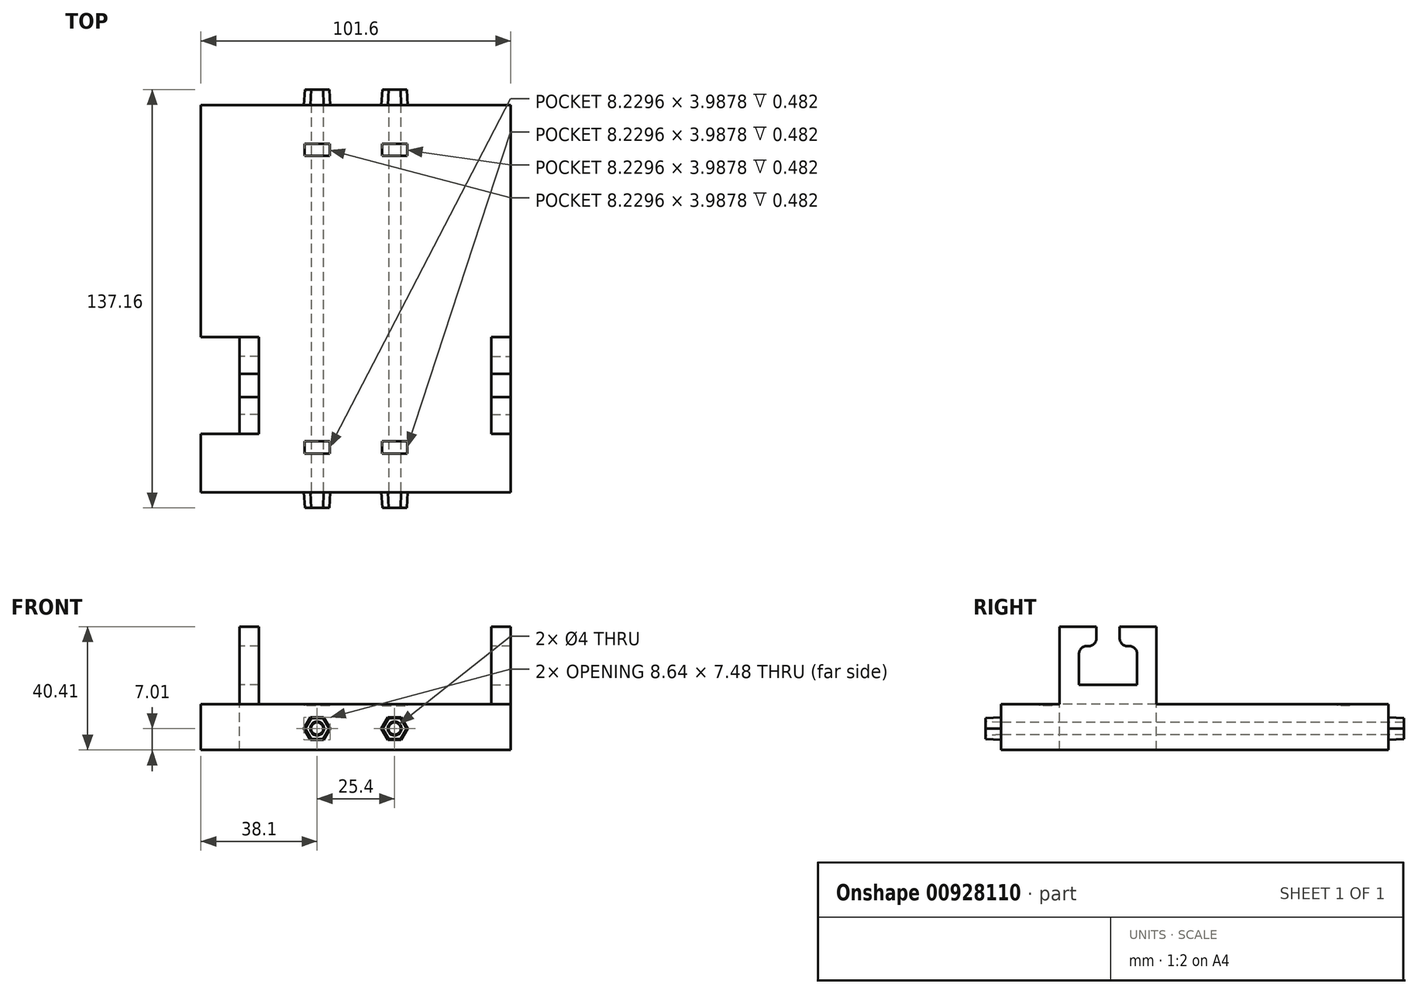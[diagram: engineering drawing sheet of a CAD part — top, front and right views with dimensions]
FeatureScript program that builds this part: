
annotation { "Feature Type Name" : "Feature", "Feature Type Description" : "" }
export const myFeature = defineFeature(function(context is Context, id is Id, definition is map)
    precondition{}
    {
        {
            var Q0;
            Q0=qCreatedBy(makeId("Top.planeOp"),FACE);
            var sketch = newSketch(context, id + "F0", { "sketchPlane" : qUnion([Q0])});
            skLineSegment(sketch, "E0.bottom", {"start": v(-50.8, 0) * mm, "end": v(50.8, 0) * mm});
            skLineSegment(sketch, "E0.top", {"start": v(-50.8, -127) * mm, "end": v(50.8, -127) * mm});
            skLineSegment(sketch, "E0.left", {"start": v(-50.8, 0) * mm, "end": v(-50.8, -127) * mm});
            skLineSegment(sketch, "E0.right", {"start": v(50.8, 0) * mm, "end": v(50.8, -127) * mm});
            skSolve(sketch);
        }
        {
            var Q0;
            Q0 = qSketchRegion(id + "F0", true);
            extrude(context, id + "F1", {"entities" : qUnion([Q0]), "depth" : 15 * mm, "offsetDistance" : 25.4 * mm});
        }
        {
            var Q0;
            Q0=makeQuery(id+"F1.opExtrude","SWEPT_FACE",FACE,{"disambiguationData":[OSD([sQuery(id+"F0.wireOp",EDGE,"E0.bottom")])]});
            var sketch = newSketch(context, id + "F2", { "sketchPlane" : qUnion([Q0])});
            skCircle(sketch, "E1", {"center": v(12.7, 7.01) * mm, "radius": 2 * mm});
            skCircle(sketch, "E2", {"center": v(-12.7, 7.01) * mm, "radius": 2 * mm});
            skPoint(sketch, "E3", {"position": v(-50.8, 7.5) * mm});
            skLineSegment(sketch, "E4", {"start": v(-12.7, 7.01) * mm, "end": v(12.7, 7.01) * mm, "construction": true});
            skLineSegment(sketch, "E5", {"start": v(0, 7.01) * mm, "end": v(0, 15.01) * mm, "construction": true});
            skSolve(sketch);
        }
        {
            var Q0;
            Q0=makeQuery(id+"F1.opExtrude","SWEPT_FACE",FACE,{"disambiguationData":[OSD([sQuery(id+"F0.wireOp",EDGE,"E0.bottom")])]});
            var sketch = newSketch(context, id + "F3", { "sketchPlane" : qUnion([Q0])});
            skCircle(sketch, "E6.cCircle", {"center": v(-12.7, 7.01) * mm, "radius": 3.74 * mm, "construction": true});
            skLineSegment(sketch, "E6.0", {"start": v(-8.38, 7.01) * mm, "end": v(-10.54, 3.27) * mm});
            skLineSegment(sketch, "E6.1", {"start": v(-10.54, 3.27) * mm, "end": v(-14.86, 3.27) * mm});
            skLineSegment(sketch, "E6.2", {"start": v(-14.86, 3.27) * mm, "end": v(-17.02, 7.01) * mm});
            skLineSegment(sketch, "E6.3", {"start": v(-17.02, 7.01) * mm, "end": v(-14.86, 10.75) * mm});
            skLineSegment(sketch, "E6.4", {"start": v(-14.86, 10.75) * mm, "end": v(-10.54, 10.75) * mm});
            skLineSegment(sketch, "E6.5", {"start": v(-10.54, 10.75) * mm, "end": v(-8.38, 7.01) * mm});
            skPoint(sketch, "E6.0.midPoint", {"position": v(-9.46, 5.14) * mm});
            skCircle(sketch, "E7.cCircle", {"center": v(12.7, 7.01) * mm, "radius": 3.74 * mm, "construction": true});
            skLineSegment(sketch, "E7.0", {"start": v(17.02, 7.01) * mm, "end": v(14.86, 3.27) * mm});
            skLineSegment(sketch, "E7.1", {"start": v(14.86, 3.27) * mm, "end": v(10.54, 3.27) * mm});
            skLineSegment(sketch, "E7.2", {"start": v(10.54, 3.27) * mm, "end": v(8.38, 7.01) * mm});
            skLineSegment(sketch, "E7.3", {"start": v(8.38, 7.01) * mm, "end": v(10.54, 10.75) * mm});
            skLineSegment(sketch, "E7.4", {"start": v(10.54, 10.75) * mm, "end": v(14.86, 10.75) * mm});
            skLineSegment(sketch, "E7.5", {"start": v(14.86, 10.75) * mm, "end": v(17.02, 7.01) * mm});
            skPoint(sketch, "E7.0.midPoint", {"position": v(15.94, 5.14) * mm});
            skSolve(sketch);
        }
        {
            var Q0;
            Q0=makeQuery(id+"F1.opExtrude","SWEPT_FACE",FACE,{"disambiguationData":[OSD([sQuery(id+"F0.wireOp",EDGE,"E0.top")])]});
            var sketch = newSketch(context, id + "F4", { "sketchPlane" : qUnion([Q0])});
            skCircle(sketch, "E8.cCircle", {"center": v(-12.7, 7.01) * mm, "radius": 3.74 * mm, "construction": true});
            skLineSegment(sketch, "E8.0", {"start": v(-10.54, 3.27) * mm, "end": v(-14.86, 3.27) * mm});
            skLineSegment(sketch, "E8.1", {"start": v(-14.86, 3.27) * mm, "end": v(-17.02, 7.01) * mm});
            skLineSegment(sketch, "E8.2", {"start": v(-17.02, 7.01) * mm, "end": v(-14.86, 10.75) * mm});
            skLineSegment(sketch, "E8.3", {"start": v(-14.86, 10.75) * mm, "end": v(-10.54, 10.75) * mm});
            skLineSegment(sketch, "E8.4", {"start": v(-10.54, 10.75) * mm, "end": v(-8.38, 7.01) * mm});
            skLineSegment(sketch, "E8.5", {"start": v(-8.38, 7.01) * mm, "end": v(-10.54, 3.27) * mm});
            skPoint(sketch, "E8.0.midPoint", {"position": v(-12.7, 3.27) * mm});
            skCircle(sketch, "E9.cCircle", {"center": v(12.7, 7.01) * mm, "radius": 3.74 * mm, "construction": true});
            skLineSegment(sketch, "E9.0", {"start": v(17.02, 7.01) * mm, "end": v(14.86, 3.27) * mm});
            skLineSegment(sketch, "E9.1", {"start": v(14.86, 3.27) * mm, "end": v(10.54, 3.27) * mm});
            skLineSegment(sketch, "E9.2", {"start": v(10.54, 3.27) * mm, "end": v(8.38, 7.01) * mm});
            skLineSegment(sketch, "E9.3", {"start": v(8.38, 7.01) * mm, "end": v(10.54, 10.75) * mm});
            skLineSegment(sketch, "E9.4", {"start": v(10.54, 10.75) * mm, "end": v(14.86, 10.75) * mm});
            skLineSegment(sketch, "E9.5", {"start": v(14.86, 10.75) * mm, "end": v(17.02, 7.01) * mm});
            skPoint(sketch, "E9.0.midPoint", {"position": v(15.94, 5.14) * mm});
            skCircle(sketch, "E10", {"center": v(12.7, 7.01) * mm, "radius": 2 * mm});
            skCircle(sketch, "E11", {"center": v(-12.7, 7.01) * mm, "radius": 2 * mm});
            skPoint(sketch, "E12", {"position": v(-6.45, -15) * mm});
            skLineSegment(sketch, "E13", {"start": v(-12.7, 7.01) * mm, "end": v(12.7, 7.01) * mm, "construction": true});
            skLineSegment(sketch, "E14", {"start": v(0, 7.01) * mm, "end": v(0, 15.01) * mm, "construction": true});
            skSolve(sketch);
        }
        {
            var Q0;
            Q0 = qSketchRegion(id + "F3", true);
            extrude(context, id + "F5", {"entities" : qUnion([Q0]), "operationType" : NewBodyOperationType.ADD, "depth" : 5.08 * mm, "offsetDistance" : 25.4 * mm, "hasDraft" : true, "draftAngle" : 3 * degree, "draftPullDirection" : true});
        }
        {
            var Q0;
            Q0 = qSketchRegion(id + "F4", true);
            extrude(context, id + "F6", {"entities" : qUnion([Q0]), "operationType" : NewBodyOperationType.ADD, "depth" : 5.08 * mm, "offsetDistance" : 25.4 * mm, "hasDraft" : true, "draftAngle" : 3 * degree, "draftPullDirection" : true});
        }
        {
            var Q0;
            Q0 = qSketchRegion(id + "F2", true);
            extrude(context, id + "F7", {"entities" : qUnion([Q0]), "operationType" : NewBodyOperationType.REMOVE, "endBound" : BoundingType.SYMMETRIC, "depth" : 304.8 * mm, "offsetDistance" : 25.4 * mm});
        }
        {
            var Q0;
            Q0=makeQuery(id+"F1.opExtrude","CAP_FACE",FACE,{"disambiguationData":[OSD([sQuery(id+"F0.wireOp",EDGE,"E0.bottom"),sQuery(id+"F0.wireOp",EDGE,"E0.top"),sQuery(id+"F0.wireOp",EDGE,"E0.left"),sQuery(id+"F0.wireOp",EDGE,"E0.right")])],"isStart":false});
            var sketch = newSketch(context, id + "F8", { "sketchPlane" : qUnion([Q0])});
            skLineSegment(sketch, "E15.bottom", {"start": v(-8.59, -110.31) * mm, "end": v(-16.81, -110.31) * mm});
            skLineSegment(sketch, "E15.top", {"start": v(-8.59, -114.3) * mm, "end": v(-16.81, -114.3) * mm});
            skLineSegment(sketch, "E15.left", {"start": v(-8.59, -110.31) * mm, "end": v(-8.59, -114.3) * mm});
            skLineSegment(sketch, "E15.right", {"start": v(-16.81, -110.31) * mm, "end": v(-16.81, -114.3) * mm});
            skPoint(sketch, "E15.middle", {"position": v(-12.7, -112.3) * mm});
            skLineSegment(sketch, "E16.bottom", {"start": v(8.59, -110.31) * mm, "end": v(16.81, -110.31) * mm});
            skLineSegment(sketch, "E16.top", {"start": v(8.59, -114.3) * mm, "end": v(16.81, -114.3) * mm});
            skLineSegment(sketch, "E16.left", {"start": v(8.59, -110.31) * mm, "end": v(8.59, -114.3) * mm});
            skLineSegment(sketch, "E16.right", {"start": v(16.81, -110.31) * mm, "end": v(16.81, -114.3) * mm});
            skPoint(sketch, "E16.middle", {"position": v(12.7, -112.3) * mm});
            skLineSegment(sketch, "E17.bottom", {"start": v(8.59, -12.7) * mm, "end": v(16.81, -12.7) * mm});
            skLineSegment(sketch, "E17.top", {"start": v(8.59, -16.69) * mm, "end": v(16.81, -16.69) * mm});
            skLineSegment(sketch, "E17.left", {"start": v(8.59, -12.7) * mm, "end": v(8.59, -16.69) * mm});
            skLineSegment(sketch, "E17.right", {"start": v(16.81, -12.7) * mm, "end": v(16.81, -16.69) * mm});
            skPoint(sketch, "E17.middle", {"position": v(12.7, -14.7) * mm});
            skLineSegment(sketch, "E18.bottom", {"start": v(-8.59, -12.7) * mm, "end": v(-16.81, -12.7) * mm});
            skLineSegment(sketch, "E18.top", {"start": v(-8.59, -16.69) * mm, "end": v(-16.81, -16.69) * mm});
            skLineSegment(sketch, "E18.left", {"start": v(-8.59, -12.7) * mm, "end": v(-8.59, -16.69) * mm});
            skLineSegment(sketch, "E18.right", {"start": v(-16.81, -12.7) * mm, "end": v(-16.81, -16.69) * mm});
            skPoint(sketch, "E18.middle", {"position": v(-12.7, -14.7) * mm});
            skLineSegment(sketch, "E19", {"start": v(0, -127) * mm, "end": v(0, 0) * mm});
            skSolve(sketch);
        }
        {
            var Q0;
            Q0 = qSketchRegion(id + "F8", true);
            extrude(context, id + "F9", {"entities" : qUnion([Q0]), "operationType" : NewBodyOperationType.REMOVE, "oppositeDirection" : true, "depth" : ((.374 / 2) + (.591 / 2)) * mm, "offsetDistance" : 25.4 * mm});
        }
        {
            var Q0;
            Q0=makeQuery(id+"F1.opExtrude","SWEPT_FACE",FACE,{"disambiguationData":[OSD([sQuery(id+"F0.wireOp",EDGE,"E0.right")])]});
            var sketch = newSketch(context, id + "F10", { "sketchPlane" : qUnion([Q0])});
            skLineSegment(sketch, "E20.bottom", {"start": v(-76.1, 0) * mm, "end": v(-107.85, 0) * mm});
            skLineSegment(sketch, "E20.top", {"start": v(-76.1, 40.41) * mm, "end": v(-107.85, 40.41) * mm});
            skLineSegment(sketch, "E20.left", {"start": v(-76.1, 0) * mm, "end": v(-76.1, 40.41) * mm});
            skLineSegment(sketch, "E20.right", {"start": v(-107.85, 0) * mm, "end": v(-107.85, 40.41) * mm});
            skSolve(sketch);
        }
        {
            var Q0;
            Q0 = qSketchRegion(id + "F10", true);
            extrude(context, id + "F11", {"entities" : qUnion([Q0]), "operationType" : NewBodyOperationType.ADD, "oppositeDirection" : true, "depth" : 6.35 * mm, "offsetDistance" : 25.4 * mm});
        }
        {
            var Q0;
            Q0=makeQuery(id+"F11.boolean.opBoolean","MERGE",FACE,{"derivedFrom":[makeQuery(id+"F1.opExtrude","SWEPT_FACE",FACE,{"disambiguationData":[OSD([sQuery(id+"F0.wireOp",EDGE,"E0.right")])]}),makeQuery(id+"F11.opExtrude","CAP_FACE",FACE,{"disambiguationData":[OSD([sQuery(id+"F10.wireOp",EDGE,"E20.bottom"),sQuery(id+"F10.wireOp",EDGE,"E20.top"),sQuery(id+"F10.wireOp",EDGE,"E20.left"),sQuery(id+"F10.wireOp",EDGE,"E20.right")])],"isStart":true})]});
            var sketch = newSketch(context, id + "F12", { "sketchPlane" : qUnion([Q0])});
            skLineSegment(sketch, "E21.bottom", {"start": v(-101.5, 34.06) * mm, "end": v(-82.45, 34.06) * mm});
            skLineSegment(sketch, "E21.top", {"start": v(-101.5, 21.36) * mm, "end": v(-82.45, 21.36) * mm});
            skLineSegment(sketch, "E21.left", {"start": v(-101.5, 34.06) * mm, "end": v(-101.5, 21.36) * mm});
            skLineSegment(sketch, "E21.right", {"start": v(-82.45, 34.06) * mm, "end": v(-82.45, 21.36) * mm});
            skLineSegment(sketch, "E22", {"start": v(-101.5, 27.71) * mm, "end": v(-107.85, 27.71) * mm});
            skLineSegment(sketch, "E23", {"start": v(-82.45, 27.71) * mm, "end": v(-76.1, 27.71) * mm});
            skSolve(sketch);
        }
        {
            var Q0;
            Q0 = qSketchRegion(id + "F12", true);
            extrude(context, id + "F13", {"entities" : qUnion([Q0]), "operationType" : NewBodyOperationType.REMOVE, "oppositeDirection" : true, "depth" : 25.4 * mm, "offsetDistance" : 25.4 * mm});
        }
        {
            var Q0;
            Q0=makeQuery(id+"F11.boolean.opBoolean","MERGE",FACE,{"derivedFrom":[makeQuery(id+"F1.opExtrude","SWEPT_FACE",FACE,{"disambiguationData":[OSD([sQuery(id+"F0.wireOp",EDGE,"E0.right")])]}),makeQuery(id+"F11.opExtrude","CAP_FACE",FACE,{"disambiguationData":[OSD([sQuery(id+"F10.wireOp",EDGE,"E20.bottom"),sQuery(id+"F10.wireOp",EDGE,"E20.top"),sQuery(id+"F10.wireOp",EDGE,"E20.left"),sQuery(id+"F10.wireOp",EDGE,"E20.right")])],"isStart":true})]});
            var sketch = newSketch(context, id + "F14", { "sketchPlane" : qUnion([Q0])});
            skLineSegment(sketch, "E24", {"start": v(-82.45, 34.06) * mm, "end": v(-101.5, 21.36) * mm});
            skLineSegment(sketch, "E25", {"start": v(-101.5, 34.06) * mm, "end": v(-91.97, 27.71) * mm});
            skLineSegment(sketch, "E26", {"start": v(-91.97, 27.71) * mm, "end": v(-82.45, 21.36) * mm});
            skSolve(sketch);
        }
        {
            var Q0;
            Q0=makeQuery(id+"F1.opExtrude","CAP_FACE",FACE,{"disambiguationData":[OSD([sQuery(id+"F0.wireOp",EDGE,"E0.bottom"),sQuery(id+"F0.wireOp",EDGE,"E0.top"),sQuery(id+"F0.wireOp",EDGE,"E0.left"),sQuery(id+"F0.wireOp",EDGE,"E0.right")])],"isStart":false});
            var sketch = newSketch(context, id + "F15", { "sketchPlane" : qUnion([Q0])});
            skLineSegment(sketch, "E27.bottom", {"start": v(-50.8, -107.85) * mm, "end": v(-38.1, -107.85) * mm});
            skLineSegment(sketch, "E27.top", {"start": v(-50.8, -76.1) * mm, "end": v(-38.1, -76.1) * mm});
            skLineSegment(sketch, "E27.left", {"start": v(-50.8, -107.85) * mm, "end": v(-50.8, -76.1) * mm});
            skLineSegment(sketch, "E27.right", {"start": v(-38.1, -107.85) * mm, "end": v(-38.1, -76.1) * mm});
            skSolve(sketch);
        }
        {
            var Q0;
            Q0 = qSketchRegion(id + "F15", true);
            extrude(context, id + "F16", {"entities" : qUnion([Q0]), "operationType" : NewBodyOperationType.REMOVE, "endBound" : BoundingType.SYMMETRIC, "oppositeDirection" : true, "depth" : 50.8 * mm, "offsetDistance" : 25.4 * mm});
        }
        {
            var Q0;
            Q0=makeQuery(id+"F1.opExtrude","CAP_FACE",FACE,{"disambiguationData":[OSD([sQuery(id+"F0.wireOp",EDGE,"E0.bottom"),sQuery(id+"F0.wireOp",EDGE,"E0.top"),sQuery(id+"F0.wireOp",EDGE,"E0.left"),sQuery(id+"F0.wireOp",EDGE,"E0.right")])],"isStart":false});
            var sketch = newSketch(context, id + "F17", { "sketchPlane" : qUnion([Q0])});
            skLineSegment(sketch, "E28.bottom", {"start": v(-38.1, -76.1) * mm, "end": v(-31.75, -76.1) * mm});
            skLineSegment(sketch, "E28.top", {"start": v(-38.1, -107.85) * mm, "end": v(-31.75, -107.85) * mm});
            skLineSegment(sketch, "E28.left", {"start": v(-38.1, -76.1) * mm, "end": v(-38.1, -107.85) * mm});
            skLineSegment(sketch, "E28.right", {"start": v(-31.75, -76.1) * mm, "end": v(-31.75, -107.85) * mm});
            skSolve(sketch);
        }
        {
            var Q0;
            Q0 = qSketchRegion(id + "F17", true);
            var Q1;
            Q1=makeQuery(id+"F11.opExtrude","SWEPT_FACE",FACE,{"disambiguationData":[OSD([sQuery(id+"F10.wireOp",EDGE,"E20.top")])]});
            extrude(context, id + "F18", {"entities" : qUnion([Q0]), "operationType" : NewBodyOperationType.ADD, "endBound" : BoundingType.UP_TO_SURFACE, "depth" : 25.4 * mm, "endBoundEntityFace" : qUnion([Q1]), "offsetDistance" : 25.4 * mm});
        }
        {
            var Q0;
            Q0=makeQuery(id+"F18.boolean.opBoolean","MERGE",FACE,{"derivedFrom":[makeQuery(id+"F16.boolean.opBoolean","COPY",FACE,{"derivedFrom":makeQuery(id+"F16.opExtrude","SWEPT_FACE",FACE,{"disambiguationData":[OSD([sQuery(id+"F15.wireOp",EDGE,"E27.right")])]})}),makeQuery(id+"F18.opExtrude","SWEPT_FACE",FACE,{"disambiguationData":[OSD([sQuery(id+"F17.wireOp",EDGE,"E28.left")])]})]});
            var sketch = newSketch(context, id + "F19", { "sketchPlane" : qUnion([Q0])});
            skLineSegment(sketch, "E29.bottom", {"start": v(82.45, 34.06) * mm, "end": v(101.5, 34.06) * mm});
            skLineSegment(sketch, "E29.top", {"start": v(82.45, 21.36) * mm, "end": v(101.5, 21.36) * mm});
            skLineSegment(sketch, "E29.left", {"start": v(82.45, 34.06) * mm, "end": v(82.45, 21.36) * mm});
            skLineSegment(sketch, "E29.right", {"start": v(101.5, 34.06) * mm, "end": v(101.5, 21.36) * mm});
            skSolve(sketch);
        }
        {
            var Q0;
            Q0 = qSketchRegion(id + "F19", true);
            extrude(context, id + "F20", {"entities" : qUnion([Q0]), "operationType" : NewBodyOperationType.REMOVE, "oppositeDirection" : true, "depth" : 25.4 * mm, "offsetDistance" : 25.4 * mm});
        }
        {
            var Q0;
            Q0=makeQuery(id+"F18.opExtrude","CAP_FACE",FACE,{"disambiguationData":[OSD([sQuery(id+"F17.wireOp",EDGE,"E28.bottom"),sQuery(id+"F17.wireOp",EDGE,"E28.top"),sQuery(id+"F17.wireOp",EDGE,"E28.left"),sQuery(id+"F17.wireOp",EDGE,"E28.right")])],"isStart":false});
            var sketch = newSketch(context, id + "F21", { "sketchPlane" : qUnion([Q0])});
            skLineSegment(sketch, "E30.bottom", {"start": v(-38.1, -88.16) * mm, "end": v(50.8, -88.16) * mm});
            skLineSegment(sketch, "E30.top", {"start": v(-38.1, -95.78) * mm, "end": v(50.8, -95.78) * mm});
            skLineSegment(sketch, "E30.left", {"start": v(-38.1, -88.16) * mm, "end": v(-38.1, -95.78) * mm});
            skLineSegment(sketch, "E30.right", {"start": v(50.8, -88.16) * mm, "end": v(50.8, -95.78) * mm});
            skSolve(sketch);
        }
        {
            var Q0;
            Q0 = qSketchRegion(id + "F21", true);
            extrude(context, id + "F22", {"entities" : qUnion([Q0]), "operationType" : NewBodyOperationType.REMOVE, "oppositeDirection" : true, "depth" : 7.62 * mm, "offsetDistance" : 25.4 * mm});
        }
        {
            var Q0;
            Q0=makeQuery(id+"F20.boolean.opBoolean","COPY",EDGE,{"derivedFrom":makeQuery(id+"F20.opExtrude","SWEPT_EDGE",EDGE,{"disambiguationData":[OSD([sQuery(id+"F19.wireOp",EDGE,"E29.bottom"),sQuery(id+"F19.wireOp",EDGE,"E29.left")])]})});
            var Q1;
            Q1=makeQuery(id+"F20.boolean.opBoolean","COPY",EDGE,{"derivedFrom":makeQuery(id+"F20.opExtrude","SWEPT_EDGE",EDGE,{"disambiguationData":[OSD([sQuery(id+"F19.wireOp",EDGE,"E29.bottom"),sQuery(id+"F19.wireOp",EDGE,"E29.right")])]})});
            var Q2;
            Q2=makeQuery(id+"F13.boolean.opBoolean","COPY",EDGE,{"derivedFrom":makeQuery(id+"F13.opExtrude","SWEPT_EDGE",EDGE,{"disambiguationData":[OSD([sQuery(id+"F12.wireOp",EDGE,"E21.bottom"),sQuery(id+"F12.wireOp",EDGE,"E21.left")])]})});
            var Q3;
            Q3=makeQuery(id+"F13.boolean.opBoolean","COPY",EDGE,{"derivedFrom":makeQuery(id+"F13.opExtrude","SWEPT_EDGE",EDGE,{"disambiguationData":[OSD([sQuery(id+"F12.wireOp",EDGE,"E21.bottom"),sQuery(id+"F12.wireOp",EDGE,"E21.right")])]})});
            var Q4;
            Q4=makeQuery(id+"F22.boolean.opBoolean","INTERSECT",EDGE,{"derivedFrom":[makeQuery(id+"F13.boolean.opBoolean","COPY",FACE,{"derivedFrom":makeQuery(id+"F13.opExtrude","SWEPT_FACE",FACE,{"disambiguationData":[OSD([sQuery(id+"F12.wireOp",EDGE,"E21.bottom")])]})}),makeQuery(id+"F22.opExtrude","SWEPT_FACE",FACE,{"disambiguationData":[OSD([sQuery(id+"F21.wireOp",EDGE,"E30.top")])]})]});
            var Q5;
            Q5=makeQuery(id+"F22.boolean.opBoolean","INTERSECT",EDGE,{"derivedFrom":[makeQuery(id+"F13.boolean.opBoolean","COPY",FACE,{"derivedFrom":makeQuery(id+"F13.opExtrude","SWEPT_FACE",FACE,{"disambiguationData":[OSD([sQuery(id+"F12.wireOp",EDGE,"E21.bottom")])]})}),makeQuery(id+"F22.opExtrude","SWEPT_FACE",FACE,{"disambiguationData":[OSD([sQuery(id+"F21.wireOp",EDGE,"E30.bottom")])]})]});
            var Q6;
            Q6=makeQuery(id+"F22.boolean.opBoolean","INTERSECT",EDGE,{"derivedFrom":[makeQuery(id+"F20.boolean.opBoolean","COPY",FACE,{"derivedFrom":makeQuery(id+"F20.opExtrude","SWEPT_FACE",FACE,{"disambiguationData":[OSD([sQuery(id+"F19.wireOp",EDGE,"E29.bottom")])]})}),makeQuery(id+"F22.opExtrude","SWEPT_FACE",FACE,{"disambiguationData":[OSD([sQuery(id+"F21.wireOp",EDGE,"E30.bottom")])]})]});
            var Q7;
            Q7=makeQuery(id+"F22.boolean.opBoolean","INTERSECT",EDGE,{"derivedFrom":[makeQuery(id+"F20.boolean.opBoolean","COPY",FACE,{"derivedFrom":makeQuery(id+"F20.opExtrude","SWEPT_FACE",FACE,{"disambiguationData":[OSD([sQuery(id+"F19.wireOp",EDGE,"E29.bottom")])]})}),makeQuery(id+"F22.opExtrude","SWEPT_FACE",FACE,{"disambiguationData":[OSD([sQuery(id+"F21.wireOp",EDGE,"E30.top")])]})]});
            fillet(context, id + "F23", {"entities" : qUnion([Q0, Q1, Q2, Q3, Q4, Q5, Q6, Q7]), "radius" : 2.54 * mm, "allowEdgeOverflow" : false});
        }
    });
